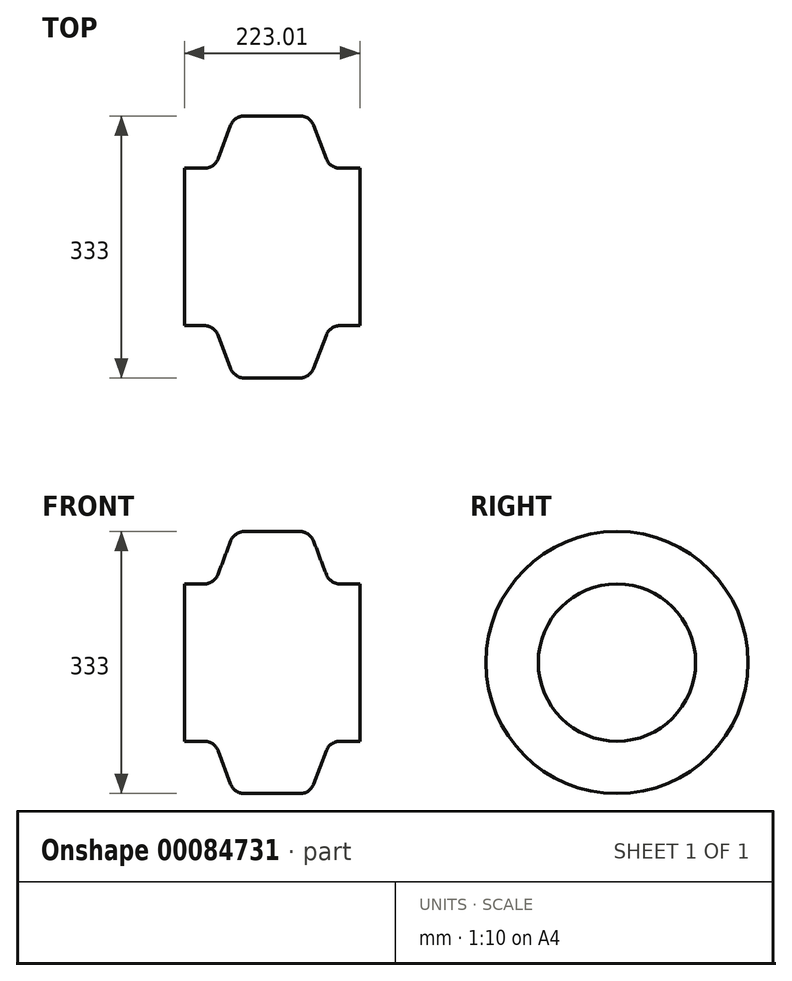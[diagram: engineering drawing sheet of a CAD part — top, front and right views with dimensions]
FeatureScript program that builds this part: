
annotation { "Feature Type Name" : "Feature", "Feature Type Description" : "" }
export const myFeature = defineFeature(function(context is Context, id is Id, definition is map)
    precondition{}
    {
        {
            var Q0;
            Q0=qCreatedBy(makeId("Top.planeOp"),FACE);
            var sketch = newSketch(context, id + "F0", { "sketchPlane" : qUnion([Q0])});
            skLineSegment(sketch, "E0.bottom", {"start": v(-91.34, 0) * mm, "end": v(131.67, 0) * mm, "construction": true});
            skLineSegment(sketch, "E0.left", {"start": v(-91.34, 0) * mm, "end": v(-91.34, -99.95) * mm});
            skLineSegment(sketch, "E0.right", {"start": v(131.67, 0) * mm, "end": v(131.67, -99.95) * mm});
            skPoint(sketch, "E1", {"position": v(-65.94, -99.95) * mm});
            skPoint(sketch, "E2", {"position": v(106.27, -99.95) * mm});
            skPoint(sketch, "E3", {"position": v(89.04, -111.81) * mm});
            skPoint(sketch, "E4", {"position": v(72.7, -154.63) * mm});
            skPoint(sketch, "E5", {"position": v(55.47, -166.5) * mm});
            skPoint(sketch, "E6", {"position": v(-15.14, -166.5) * mm});
            skPoint(sketch, "E7", {"position": v(-32.37, -154.63) * mm});
            skPoint(sketch, "E8", {"position": v(-48.71, -111.81) * mm});
            skArc(sketch, "E9", {"start": v(-48.71, -111.81) * mm, "mid": v(-55.48, -103.2) * mm, "end": v(-65.94, -99.95) * mm});
            skLineSegment(sketch, "E10", {"start": v(-65.94, -99.95) * mm, "end": v(-91.34, -99.95) * mm});
            skLineSegment(sketch, "E11", {"start": v(-48.71, -111.81) * mm, "end": v(-32.37, -154.63) * mm});
            skArc(sketch, "E12", {"start": v(-32.37, -154.63) * mm, "mid": v(-25.6, -163.24) * mm, "end": v(-15.14, -166.5) * mm});
            skLineSegment(sketch, "E13", {"start": v(106.27, -99.95) * mm, "end": v(131.67, -99.95) * mm});
            skLineSegment(sketch, "E14", {"start": v(89.04, -111.81) * mm, "end": v(72.7, -154.63) * mm});
            skArc(sketch, "E15", {"start": v(106.27, -99.95) * mm, "mid": v(95.8, -103.2) * mm, "end": v(89.04, -111.81) * mm});
            skArc(sketch, "E16", {"start": v(55.47, -166.5) * mm, "mid": v(65.93, -163.24) * mm, "end": v(72.7, -154.63) * mm});
            skLineSegment(sketch, "E17", {"start": v(-15.14, -166.5) * mm, "end": v(55.47, -166.5) * mm});
            skLineSegment(sketch, "E18", {"start": v(-91.34, 0) * mm, "end": v(131.67, 0) * mm});
            skSolve(sketch);
        }
        {
            var Q0;
            Q0 = qSketchRegion(id + "F0", true);
            var Q1;
            Q1=sQuery(id+"F0.wireOp",EDGE,"E18");
            revolve(context, id + "F1", {"entities" : qUnion([Q0]), "axis" : qUnion([Q1]), "revolveType" : RevolveType.FULL});
        }
    });
